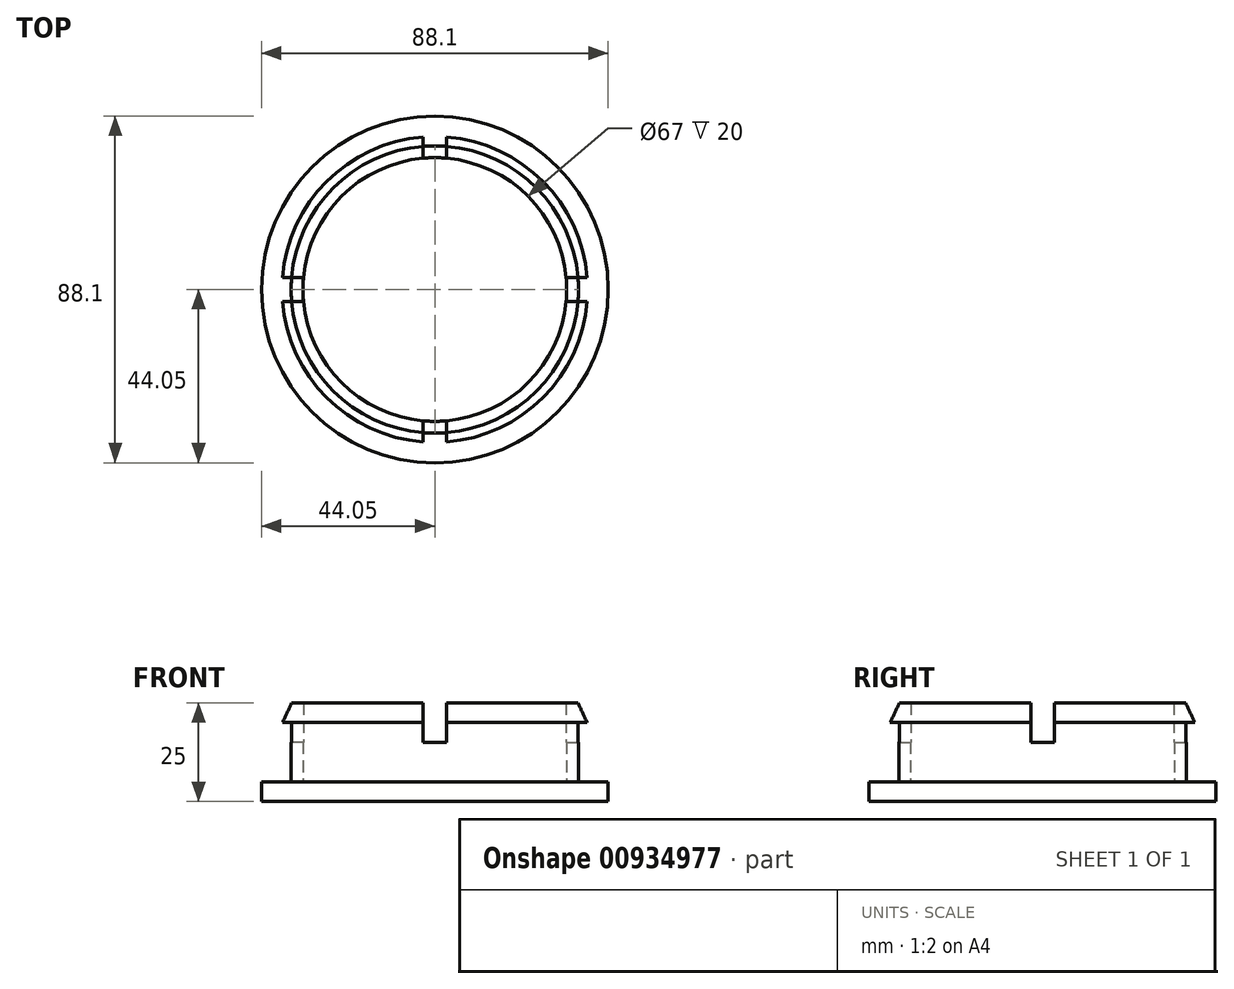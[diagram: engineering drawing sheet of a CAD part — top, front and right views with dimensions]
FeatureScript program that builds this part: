
annotation { "Feature Type Name" : "Feature", "Feature Type Description" : "" }
export const myFeature = defineFeature(function(context is Context, id is Id, definition is map)
    precondition{}
    {
        {
            var Q0;
            Q0=qCreatedBy(makeId("Top.planeOp"),FACE);
            var sketch = newSketch(context, id + "F0", { "sketchPlane" : qUnion([Q0])});
            skCircle(sketch, "E0", {"center": v(0, 0) * mm, "radius": 36.5 * mm});
            skCircle(sketch, "E1.0", {"center": v(0, 0) * mm, "radius": 33.5 * mm});
            skSolve(sketch);
        }
        {
            var Q0;
            Q0 = qSketchRegion(id + "F0", true);
            extrude(context, id + "F1", {"entities" : qUnion([Q0]), "depth" : 20 * mm, "offsetDistance" : 25 * mm});
        }
        {
            var Q0;
            Q0=makeQuery(id+"F1.opExtrude","CAP_FACE",FACE,{"disambiguationData":[OSD([sQuery(id+"F0.wireOp",EDGE,"E0"),sQuery(id+"F0.wireOp",EDGE,"E1.0")])],"isStart":false});
            var sketch = newSketch(context, id + "F2", { "sketchPlane" : qUnion([Q0])});
            skCircle(sketch, "E2.0", {"center": v(0, 0) * mm, "radius": 36.5 * mm});
            skSolve(sketch);
        }
        {
            var Q0;
            Q0 = qSketchRegion(id + "F2", true);
            extrude(context, id + "F3", {"entities" : qUnion([Q0]), "operationType" : NewBodyOperationType.ADD, "oppositeDirection" : true, "depth" : 5 * mm, "offsetDistance" : 25 * mm, "hasDraft" : true, "draftAngle" : 25 * degree});
        }
        {
            var Q0;
            Q0=makeQuery(id+"F3.boolean.opBoolean","SPLIT",FACE,{"disambiguationData":[TD([makeQuery(id+"F1.opExtrude","SWEPT_FACE",FACE,{"disambiguationData":[OSD([sQuery(id+"F0.wireOp",EDGE,"E1.0")])]})])],"derivedFrom":makeQuery(id+"F3.opExtrude","CAP_FACE",FACE,{"disambiguationData":[OSD([sQuery(id+"F2.wireOp",EDGE,"E2.0")])],"isStart":false})});
            var sketch = newSketch(context, id + "F4", { "sketchPlane" : qUnion([Q0])});
            skSolve(sketch);
        }
        {
            var Q0;
            Q0 = qSketchRegion(id + "F4", true);
            var Q1;
            Q1=makeQuery(id+"F4.imprint","IMPRINT",FACE,{"disambiguationData":[TD([[makeQuery(id+"F4.imprint","IMPRINT",EDGE,{"derivedFrom":makeQuery(id+"F3.boolean.opBoolean","INTERSECT",EDGE,{"derivedFrom":[makeQuery(id+"F1.opExtrude","SWEPT_FACE",FACE,{"disambiguationData":[OSD([sQuery(id+"F0.wireOp",EDGE,"E1.0")])]}),makeQuery(id+"F3.opExtrude","CAP_FACE",FACE,{"disambiguationData":[OSD([sQuery(id+"F2.wireOp",EDGE,"E2.0")])],"isStart":false})]})}),-1.0]])]});
            extrude(context, id + "F5", {"entities" : qUnion([Q0, Q1]), "operationType" : NewBodyOperationType.REMOVE, "oppositeDirection" : true, "depth" : 25 * mm, "offsetDistance" : 25 * mm});
        }
        {
            var Q0;
            Q0=makeQuery(id+"F1.opExtrude","CAP_FACE",FACE,{"disambiguationData":[OSD([sQuery(id+"F0.wireOp",EDGE,"E0"),sQuery(id+"F0.wireOp",EDGE,"E1.0")])],"isStart":true});
            var sketch = newSketch(context, id + "F6", { "sketchPlane" : qUnion([Q0])});
            skCircle(sketch, "E3.0", {"center": v(0, 0) * mm, "radius": 44.05 * mm});
            skSolve(sketch);
        }
        {
            var Q0;
            Q0 = qSketchRegion(id + "F6", true);
            extrude(context, id + "F7", {"entities" : qUnion([Q0]), "operationType" : NewBodyOperationType.ADD, "depth" : 5 * mm, "offsetDistance" : 25 * mm});
        }
        {
            var Q0;
            Q0=makeQuery(id+"F7.boolean.opBoolean","SPLIT",FACE,{"disambiguationData":[TD([makeQuery(id+"F1.opExtrude","SWEPT_FACE",FACE,{"disambiguationData":[OSD([sQuery(id+"F0.wireOp",EDGE,"E1.0")])]})])],"derivedFrom":makeQuery(id+"F7.opExtrude","CAP_FACE",FACE,{"disambiguationData":[OSD([sQuery(id+"F6.wireOp",EDGE,"E3.0")])],"isStart":true})});
            var Q1;
            Q1=makeQuery(id+"F3.boolean.opBoolean","MERGE",FACE,{"derivedFrom":[makeQuery(id+"F1.opExtrude","CAP_FACE",FACE,{"disambiguationData":[OSD([sQuery(id+"F0.wireOp",EDGE,"E0"),sQuery(id+"F0.wireOp",EDGE,"E1.0")])],"isStart":false}),makeQuery(id+"F3.opExtrude","CAP_FACE",FACE,{"disambiguationData":[OSD([sQuery(id+"F2.wireOp",EDGE,"E2.0")])],"isStart":true})]});
            cPlane(context, id + "F8", {"entities" : qUnion([Q0, Q1]), "cplaneType" : CPlaneType.MID_PLANE, "offset" : 25 * mm, "width" : 150 * mm, "height" : 150 * mm});
        }
        {
            var Q0;
            Q0=qCreatedBy(id+"F8.planeOp",FACE);
            var sketch = newSketch(context, id + "F9", { "sketchPlane" : qUnion([Q0])});
            skLineSegment(sketch, "E4.1", {"start": v(3, 3) * mm, "end": v(35.05, 3) * mm});
            skArc(sketch, "E5.0", {"start": v(3, 38.38) * mm, "mid": v(0, 38.5) * mm, "end": v(-3, 38.38) * mm});
            skLineSegment(sketch, "E6.MirrorCS", {"start": v(-3, -3) * mm, "end": v(-3, -40.27) * mm});
            skLineSegment(sketch, "E7.MirrorCS", {"start": v(-3, 3) * mm, "end": v(-38.38, 3) * mm});
            skLineSegment(sketch, "E8.MirrorCS", {"start": v(-38.39, 0) * mm, "end": v(-38.5, 0) * mm});
            skLineSegment(sketch, "E9.MirrorCS", {"start": v(-3, 3) * mm, "end": v(-3, 35.05) * mm});
            skLineSegment(sketch, "E10.MirrorCS", {"start": v(-3, 3) * mm, "end": v(-38.4, 2.88) * mm});
            skLineSegment(sketch, "E11.MirrorCS", {"start": v(3, 3) * mm, "end": v(61.4, 3) * mm});
            skLineSegment(sketch, "E12.MirrorCS", {"start": v(3, 3) * mm, "end": v(3, 35.05) * mm});
            skPoint(sketch, "E13.orphan", {"position": v(-33.5, 0) * mm});
            skPoint(sketch, "E14.orphan", {"position": v(-35.05, 3) * mm});
            skPoint(sketch, "E15.orphan", {"position": v(-33.5, 2.9) * mm});
            skPoint(sketch, "E16.orphan", {"position": v(-3, -35.05) * mm});
            skPoint(sketch, "E17.orphan", {"position": v(1.55, 0) * mm});
            skPoint(sketch, "E18.end.orphan", {"position": v(35.05, 0) * mm});
            skLineSegment(sketch, "E19.bottom", {"start": v(-38.38, 3) * mm, "end": v(-3, 3) * mm});
            skLineSegment(sketch, "E19.top", {"start": v(-38.38, 3) * mm, "end": v(-3, 3) * mm});
            skLineSegment(sketch, "E19.right", {"start": v(38.38, 3) * mm, "end": v(38.38, 3) * mm});
            skPoint(sketch, "E19.middle", {"position": v(0, 3) * mm});
            skLineSegment(sketch, "E20.left", {"start": v(-3, -40.27) * mm, "end": v(-3, -3) * mm});
            skLineSegment(sketch, "E20.right", {"start": v(3, -40.27) * mm, "end": v(3, -3) * mm});
            skLineSegment(sketch, "E21.bottom", {"start": v(-61.4, 3) * mm, "end": v(-3, 3) * mm});
            skLineSegment(sketch, "E21.top", {"start": v(-61.4, 3) * mm, "end": v(-3, 3) * mm});
            skLineSegment(sketch, "E21.left", {"start": v(-61.4, 3) * mm, "end": v(-61.4, 3) * mm});
            skLineSegment(sketch, "E21.right", {"start": v(61.4, 3) * mm, "end": v(61.4, 3) * mm});
            skLineSegment(sketch, "E22.bottom", {"start": v(3, -53.78) * mm, "end": v(-3, -53.78) * mm});
            skLineSegment(sketch, "E22.top", {"start": v(3, 53.78) * mm, "end": v(-3, 53.78) * mm});
            skLineSegment(sketch, "E22.left", {"start": v(3, -53.78) * mm, "end": v(3, -3) * mm});
            skLineSegment(sketch, "E22.right", {"start": v(-3, -53.78) * mm, "end": v(-3, -3) * mm});
            skPoint(sketch, "E22.cornerSnap0", {"position": v(3, 0) * mm});
            skLineSegment(sketch, "E23.trimOffspring", {"start": v(-3, 3) * mm, "end": v(-3, 53.78) * mm});
            skLineSegment(sketch, "E24.trimOffspring", {"start": v(-3, 3) * mm, "end": v(-3, 40.27) * mm});
            skLineSegment(sketch, "E25.trimOffspring", {"start": v(3, 3) * mm, "end": v(38.38, 3) * mm});
            skLineSegment(sketch, "E26.trimOffspring", {"start": v(3, 3) * mm, "end": v(3, 53.78) * mm});
            skLineSegment(sketch, "E27.trimOffspring", {"start": v(3, 3) * mm, "end": v(3, 40.27) * mm});
            skLineSegment(sketch, "E28.bottom", {"start": v(61.4, 3) * mm, "end": v(3, 3) * mm});
            skLineSegment(sketch, "E28.top", {"start": v(61.4, -3) * mm, "end": v(3, -3) * mm});
            skLineSegment(sketch, "E28.left", {"start": v(61.4, 3) * mm, "end": v(61.4, -3) * mm});
            skLineSegment(sketch, "E28.right", {"start": v(-61.4, 3) * mm, "end": v(-61.4, -3) * mm});
            skLineSegment(sketch, "E29.trimOffspring", {"start": v(3, -3) * mm, "end": v(3, -29.05) * mm});
            skLineSegment(sketch, "E30.trimOffspring", {"start": v(-3, 3) * mm, "end": v(-61.4, 3) * mm});
            skLineSegment(sketch, "E31.trimOffspring", {"start": v(-3, -3) * mm, "end": v(-61.4, -3) * mm});
            skSolve(sketch);
        }
        {
            var Q0;
            Q0 = qSketchRegion(id + "F9", true);
            extrude(context, id + "F10", {"entities" : qUnion([Q0]), "operationType" : NewBodyOperationType.REMOVE, "depth" : 25 * mm, "offsetDistance" : 25 * mm});
        }
    });
